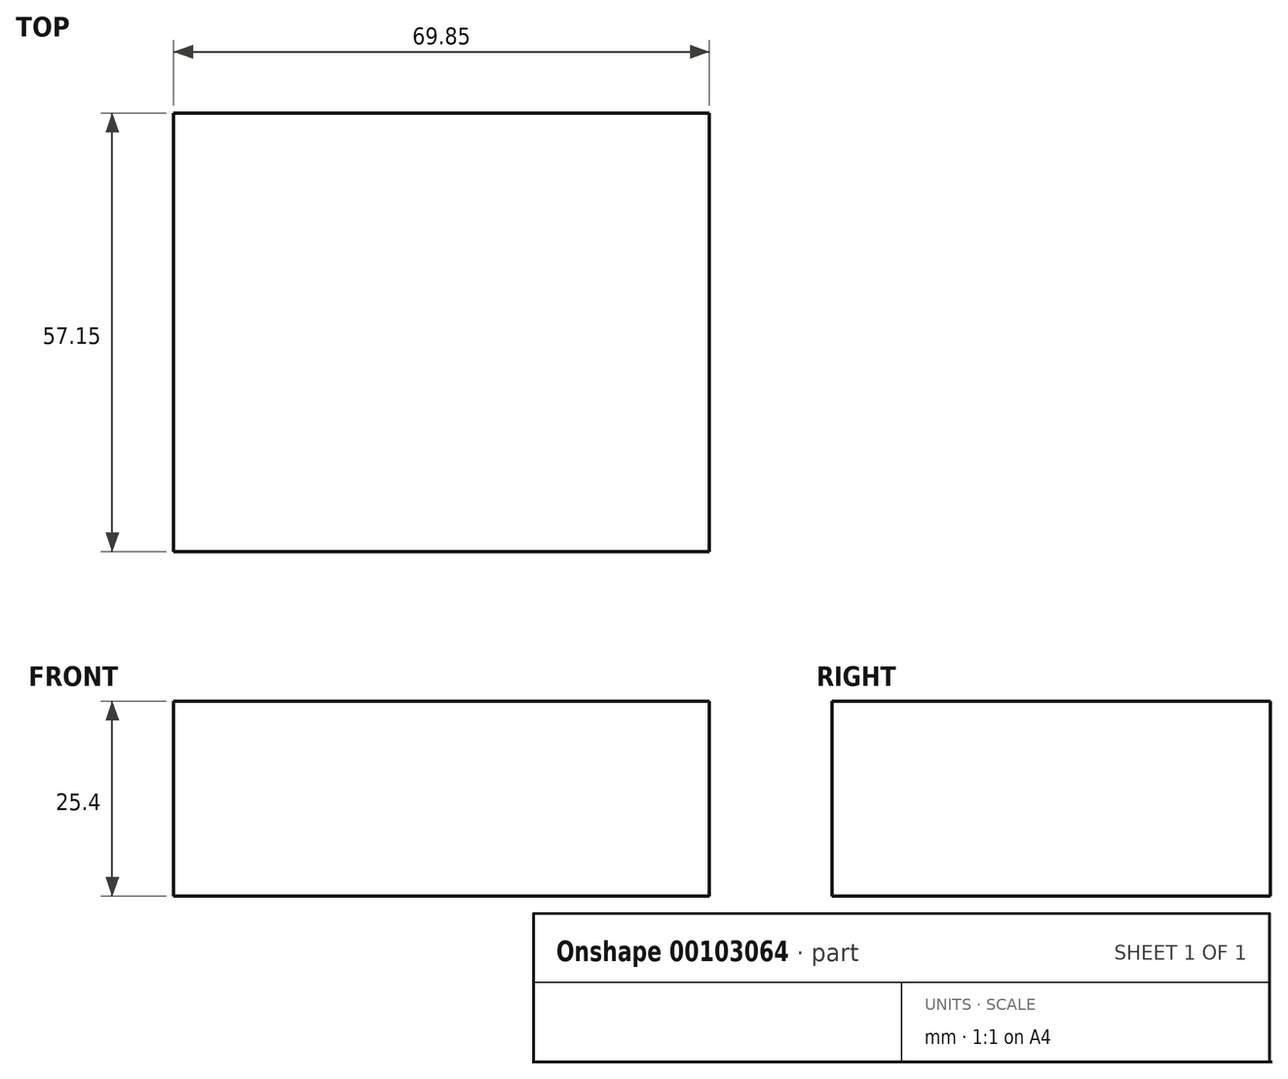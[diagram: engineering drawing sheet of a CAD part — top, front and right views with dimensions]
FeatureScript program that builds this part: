
annotation { "Feature Type Name" : "Feature", "Feature Type Description" : "" }
export const myFeature = defineFeature(function(context is Context, id is Id, definition is map)
    precondition{}
    {
        {
            var Q0;
            Q0=qCreatedBy(makeId("Top.planeOp"),FACE);
            var sketch = newSketch(context, id + "F0", { "sketchPlane" : qUnion([Q0])});
            skLineSegment(sketch, "E0.bottom", {"start": v(-70.23, 62.28) * mm, "end": v(-0.38, 62.28) * mm});
            skLineSegment(sketch, "E0.top", {"start": v(-70.23, 5.13) * mm, "end": v(-0.38, 5.13) * mm});
            skLineSegment(sketch, "E0.left", {"start": v(-70.23, 62.28) * mm, "end": v(-70.23, 5.13) * mm});
            skLineSegment(sketch, "E0.right", {"start": v(-0.38, 62.28) * mm, "end": v(-0.38, 5.13) * mm});
            skSolve(sketch);
        }
        {
            var Q0;
            Q0=makeQuery(id+"F0.imprint","IMPRINT",FACE,{"disambiguationData":[TD([[makeQuery(id+"F0.imprint","IMPRINT",EDGE,{"derivedFrom":sQuery(id+"F0.wireOp",EDGE,"E0.bottom")}),-1.0]])]});
            extrude(context, id + "F1", {"entities" : qUnion([Q0]), "depth" : 25.4 * mm});
        }
    });
